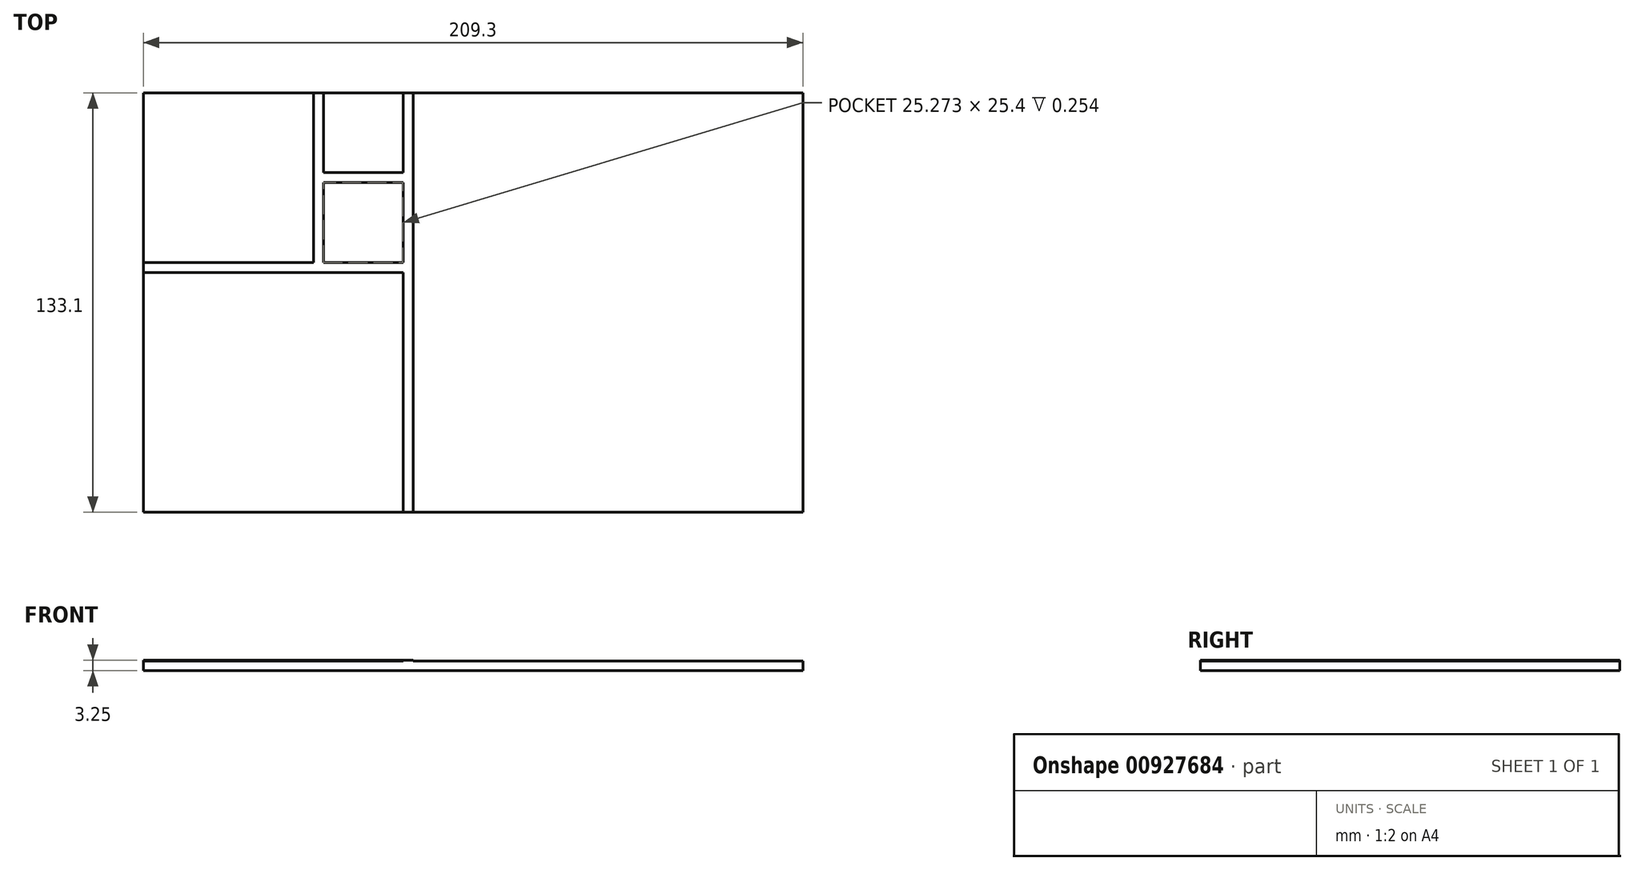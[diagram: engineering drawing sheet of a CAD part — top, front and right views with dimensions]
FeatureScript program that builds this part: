
annotation { "Feature Type Name" : "Feature", "Feature Type Description" : "" }
export const myFeature = defineFeature(function(context is Context, id is Id, definition is map)
    precondition{}
    {
        {
            var Q0;
            Q0=qCreatedBy(makeId("Top.planeOp"),FACE);
            var sketch = newSketch(context, id + "F0", { "sketchPlane" : qUnion([Q0])});
            skLineSegment(sketch, "E0.bottom", {"start": v(104.65, -66.55) * mm, "end": v(-104.65, -66.55) * mm});
            skLineSegment(sketch, "E0.top", {"start": v(104.65, 66.55) * mm, "end": v(-104.65, 66.55) * mm});
            skLineSegment(sketch, "E0.left", {"start": v(104.65, -66.55) * mm, "end": v(104.65, 66.55) * mm});
            skLineSegment(sketch, "E0.right", {"start": v(-104.65, -66.55) * mm, "end": v(-104.65, 66.55) * mm});
            skPoint(sketch, "E0.middle", {"position": v(0, 0) * mm});
            skSolve(sketch);
        }
        {
            var Q0;
            Q0=qSketchRegion(id+"F0",true);
            extrude(context, id + "F1", {"entities" : qUnion([Q0]), "depth" : 3 * mm, "offsetDistance" : 25.4 * mm});
        }
        {
            var Q0;
            Q0=makeQuery(id+"F1.opExtrude","CAP_FACE",FACE,{"disambiguationData":[OSD([sQuery(id+"F0.wireOp",EDGE,"E0.bottom"),sQuery(id+"F0.wireOp",EDGE,"E0.top"),sQuery(id+"F0.wireOp",EDGE,"E0.left"),sQuery(id+"F0.wireOp",EDGE,"E0.right")])],"isStart":false});
            var sketch = newSketch(context, id + "F2", { "sketchPlane" : qUnion([Q0])});
            skLineSegment(sketch, "E1", {"start": v(-50.67, 66.55) * mm, "end": v(-50.67, 12.7) * mm});
            skLineSegment(sketch, "E2", {"start": v(-50.67, 12.7) * mm, "end": v(-104.65, 12.7) * mm});
            skLineSegment(sketch, "E3", {"start": v(-104.65, 12.7) * mm, "end": v(-104.65, 9.52) * mm});
            skLineSegment(sketch, "E4", {"start": v(-104.65, 9.52) * mm, "end": v(-22.22, 9.53) * mm});
            skLineSegment(sketch, "E5", {"start": v(-22.22, 9.53) * mm, "end": v(-22.22, -66.55) * mm});
            skLineSegment(sketch, "E6", {"start": v(-22.22, -66.55) * mm, "end": v(-19.05, -66.55) * mm});
            skLineSegment(sketch, "E7", {"start": v(-19.05, -66.55) * mm, "end": v(-19.05, 66.55) * mm});
            skLineSegment(sketch, "E8", {"start": v(-50.67, 66.55) * mm, "end": v(-47.5, 66.55) * mm});
            skLineSegment(sketch, "E9", {"start": v(-47.5, 66.55) * mm, "end": v(-47.5, 41.28) * mm});
            skLineSegment(sketch, "E10", {"start": v(-47.5, 41.28) * mm, "end": v(-22.22, 41.28) * mm});
            skLineSegment(sketch, "E11", {"start": v(-22.22, 41.28) * mm, "end": v(-22.23, 66.55) * mm});
            skLineSegment(sketch, "E12", {"start": v(-22.22, 66.55) * mm, "end": v(-19.05, 66.55) * mm});
            skLineSegment(sketch, "E13", {"start": v(-47.5, 38.1) * mm, "end": v(-47.5, 12.7) * mm});
            skLineSegment(sketch, "E14", {"start": v(-47.5, 12.7) * mm, "end": v(-22.22, 12.7) * mm});
            skLineSegment(sketch, "E15", {"start": v(-22.22, 12.7) * mm, "end": v(-22.23, 38.1) * mm});
            skLineSegment(sketch, "E16", {"start": v(-22.23, 38.1) * mm, "end": v(-47.5, 38.1) * mm});
            skSolve(sketch);
        }
        {
            var Q0;
            Q0 = qSketchRegion(id + "F2", true);
            extrude(context, id + "F3", {"entities" : qUnion([Q0]), "operationType" : NewBodyOperationType.ADD, "depth" : 0.25 * mm, "offsetDistance" : 25.4 * mm});
        }
    });
